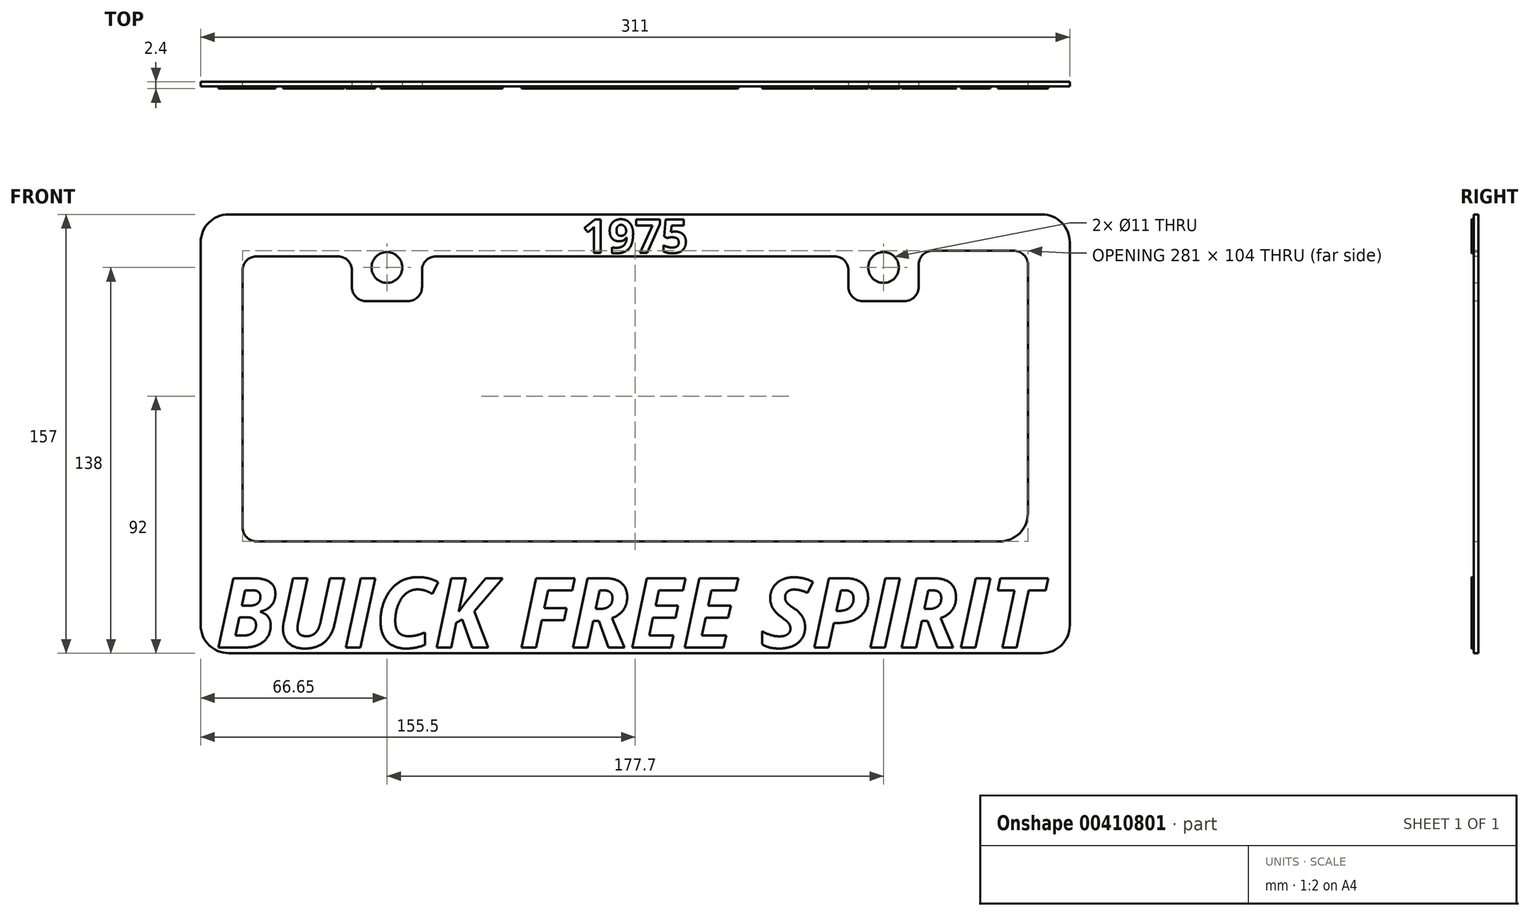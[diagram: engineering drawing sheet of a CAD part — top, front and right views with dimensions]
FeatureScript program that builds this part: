
annotation { "Feature Type Name" : "Feature", "Feature Type Description" : "" }
export const myFeature = defineFeature(function(context is Context, id is Id, definition is map)
    precondition{}
    {
        {
            var Q0;
            Q0=qCreatedBy(makeId("Front.planeOp"),FACE);
            var sketch = newSketch(context, id + "F0", { "sketchPlane" : qUnion([Q0])});
            skLineSegment(sketch, "E0.bottom", {"start": v(145.5, 78.5) * mm, "end": v(-145.5, 78.5) * mm});
            skLineSegment(sketch, "E0.top", {"start": v(145.5, -78.5) * mm, "end": v(-145.5, -78.5) * mm});
            skLineSegment(sketch, "E0.left", {"start": v(155.5, 68.5) * mm, "end": v(155.5, -68.5) * mm});
            skLineSegment(sketch, "E0.right", {"start": v(-155.5, 68.5) * mm, "end": v(-155.5, -68.5) * mm});
            skPoint(sketch, "E0.middle", {"position": v(0, 0) * mm});
            skLineSegment(sketch, "E1.bottom", {"start": v(135.5, 63.5) * mm, "end": v(-135.5, 63.5) * mm});
            skLineSegment(sketch, "E1.left", {"start": v(140.5, 58.5) * mm, "end": v(140.5, -28.5) * mm});
            skLineSegment(sketch, "E1.right", {"start": v(-140.5, 58.5) * mm, "end": v(-140.5, -33.5) * mm});
            skLineSegment(sketch, "E2", {"start": v(-135.5, -38.5) * mm, "end": v(130.5, -38.5) * mm});
            skPoint(sketch, "E3.orphan", {"position": v(140.5, -63.5) * mm});
            skPoint(sketch, "E4.orphan", {"position": v(-140.5, -63.5) * mm});
            skPoint(sketch, "E5.visualSharp", {"position": v(-155.5, 78.5) * mm});
            skArc(sketch, "E5.filletArc", {"start": v(-145.5, 78.5) * mm, "mid": v(-152.57, 75.57) * mm, "end": v(-155.5, 68.5) * mm});
            skPoint(sketch, "E6.visualSharp", {"position": v(-155.5, -78.5) * mm});
            skArc(sketch, "E6.filletArc", {"start": v(-155.5, -68.5) * mm, "mid": v(-152.57, -75.57) * mm, "end": v(-145.5, -78.5) * mm});
            skPoint(sketch, "E7.visualSharp", {"position": v(155.5, 78.5) * mm});
            skArc(sketch, "E7.filletArc", {"start": v(155.5, 68.5) * mm, "mid": v(152.57, 75.57) * mm, "end": v(145.5, 78.5) * mm});
            skPoint(sketch, "E8.visualSharp", {"position": v(155.5, -78.5) * mm});
            skArc(sketch, "E8.filletArc", {"start": v(145.5, -78.5) * mm, "mid": v(152.57, -75.57) * mm, "end": v(155.5, -68.5) * mm});
            skPoint(sketch, "E9.visualSharp", {"position": v(-140.5, 63.5) * mm});
            skArc(sketch, "E9.filletArc", {"start": v(-135.5, 63.5) * mm, "mid": v(-139.04, 62.04) * mm, "end": v(-140.5, 58.5) * mm});
            skPoint(sketch, "E10.visualSharp", {"position": v(-140.5, -38.5) * mm});
            skArc(sketch, "E10.filletArc", {"start": v(-140.5, -33.5) * mm, "mid": v(-139.04, -37.04) * mm, "end": v(-135.5, -38.5) * mm});
            skPoint(sketch, "E11.visualSharp", {"position": v(140.5, -38.5) * mm});
            skArc(sketch, "E11.filletArc", {"start": v(130.5, -38.5) * mm, "mid": v(137.57, -35.57) * mm, "end": v(140.5, -28.5) * mm});
            skPoint(sketch, "E12.visualSharp", {"position": v(140.5, 63.5) * mm});
            skArc(sketch, "E12.filletArc", {"start": v(140.5, 58.5) * mm, "mid": v(139.04, 62.04) * mm, "end": v(135.5, 63.5) * mm});
            skSolve(sketch);
        }
        {
            var Q0;
            Q0=qSketchRegion(id+"F0",true);
            extrude(context, id + "F1", {"entities" : qUnion([Q0]), "depth" : 1.6 * mm});
        }
        {
            var Q0;
            Q0=makeQuery(id+"F1.opExtrude","CAP_FACE",FACE,{"disambiguationData":[OSD([sQuery(id+"F0.wireOp",EDGE,"E0.bottom"),sQuery(id+"F0.wireOp",EDGE,"E0.top"),sQuery(id+"F0.wireOp",EDGE,"E0.left"),sQuery(id+"F0.wireOp",EDGE,"E0.right"),sQuery(id+"F0.wireOp",EDGE,"E1.bottom"),sQuery(id+"F0.wireOp",EDGE,"E1.left"),sQuery(id+"F0.wireOp",EDGE,"E1.right"),sQuery(id+"F0.wireOp",EDGE,"E2"),sQuery(id+"F0.wireOp",EDGE,"E5.filletArc"),sQuery(id+"F0.wireOp",EDGE,"E6.filletArc"),sQuery(id+"F0.wireOp",EDGE,"E7.filletArc"),sQuery(id+"F0.wireOp",EDGE,"E8.filletArc"),sQuery(id+"F0.wireOp",EDGE,"E9.filletArc"),sQuery(id+"F0.wireOp",EDGE,"E10.filletArc"),sQuery(id+"F0.wireOp",EDGE,"E11.filletArc"),sQuery(id+"F0.wireOp",EDGE,"E12.filletArc")])],"isStart":false});
            var sketch = newSketch(context, id + "F2", { "sketchPlane" : qUnion([Q0])});
            skLineSegment(sketch, "E13.bottom", {"start": v(-101.4, 63.5) * mm, "end": v(-76.3, 63.5) * mm});
            skLineSegment(sketch, "E13.top", {"start": v(-101.4, 47.5) * mm, "end": v(-76.3, 47.5) * mm});
            skLineSegment(sketch, "E13.left", {"start": v(-101.4, 63.5) * mm, "end": v(-101.4, 47.5) * mm});
            skLineSegment(sketch, "E13.right", {"start": v(-76.3, 63.5) * mm, "end": v(-76.3, 47.5) * mm});
            skLineSegment(sketch, "E14.bottom", {"start": v(76.3, 63.5) * mm, "end": v(101.4, 63.5) * mm});
            skLineSegment(sketch, "E14.top", {"start": v(76.3, 47.5) * mm, "end": v(101.4, 47.5) * mm});
            skLineSegment(sketch, "E14.left", {"start": v(76.3, 63.5) * mm, "end": v(76.3, 47.5) * mm});
            skLineSegment(sketch, "E14.right", {"start": v(101.4, 63.5) * mm, "end": v(101.4, 47.5) * mm});
            skLineSegment(sketch, "E15", {"start": v(-88.85, 47.5) * mm, "end": v(-88.85, 63.5) * mm, "construction": true});
            skLineSegment(sketch, "E16", {"start": v(-101.4, 47.5) * mm, "end": v(-140.5, 47.5) * mm, "construction": true});
            skLineSegment(sketch, "E17", {"start": v(101.4, 47.5) * mm, "end": v(140.5, 47.5) * mm, "construction": true});
            skSolve(sketch);
        }
        {
            var Q0;
            Q0=qSketchRegion(id+"F2",true);
            var Q1;
            Q1=makeQuery(id+"F1.opExtrude","CAP_FACE",FACE,{"disambiguationData":[OSD([sQuery(id+"F0.wireOp",EDGE,"E0.bottom"),sQuery(id+"F0.wireOp",EDGE,"E0.top"),sQuery(id+"F0.wireOp",EDGE,"E0.left"),sQuery(id+"F0.wireOp",EDGE,"E0.right"),sQuery(id+"F0.wireOp",EDGE,"E1.bottom"),sQuery(id+"F0.wireOp",EDGE,"E1.left"),sQuery(id+"F0.wireOp",EDGE,"E1.right"),sQuery(id+"F0.wireOp",EDGE,"E2"),sQuery(id+"F0.wireOp",EDGE,"E5.filletArc"),sQuery(id+"F0.wireOp",EDGE,"E6.filletArc"),sQuery(id+"F0.wireOp",EDGE,"E7.filletArc"),sQuery(id+"F0.wireOp",EDGE,"E8.filletArc"),sQuery(id+"F0.wireOp",EDGE,"E9.filletArc"),sQuery(id+"F0.wireOp",EDGE,"E10.filletArc"),sQuery(id+"F0.wireOp",EDGE,"E11.filletArc"),sQuery(id+"F0.wireOp",EDGE,"E12.filletArc")])],"isStart":true});
            extrude(context, id + "F3", {"entities" : qUnion([Q0]), "operationType" : NewBodyOperationType.ADD, "endBound" : BoundingType.UP_TO_SURFACE, "oppositeDirection" : true, "endBoundEntityFace" : qUnion([Q1]), "depth" : 25 * mm});
        }
        {
            var Q0;
            Q0=makeQuery(id+"F3.opExtrude","SWEPT_EDGE",EDGE,{"disambiguationData":[OSD([sQuery(id+"F2.wireOp",EDGE,"E13.top"),sQuery(id+"F2.wireOp",EDGE,"E13.left")])]});
            var Q1;
            Q1=makeQuery(id+"F3.opExtrude","SWEPT_EDGE",EDGE,{"disambiguationData":[OSD([sQuery(id+"F0.wireOp",EDGE,"E1.bottom"),sQuery(id+"F2.wireOp",EDGE,"E13.bottom"),sQuery(id+"F2.wireOp",EDGE,"E13.left")])]});
            var Q2;
            Q2=makeQuery(id+"F3.opExtrude","SWEPT_EDGE",EDGE,{"disambiguationData":[OSD([sQuery(id+"F2.wireOp",EDGE,"E13.top"),sQuery(id+"F2.wireOp",EDGE,"E13.right")])]});
            var Q3;
            Q3=makeQuery(id+"F3.opExtrude","SWEPT_EDGE",EDGE,{"disambiguationData":[OSD([sQuery(id+"F0.wireOp",EDGE,"E1.bottom"),sQuery(id+"F2.wireOp",EDGE,"E13.bottom"),sQuery(id+"F2.wireOp",EDGE,"E13.right")])]});
            var Q4;
            Q4=makeQuery(id+"F3.opExtrude","SWEPT_EDGE",EDGE,{"disambiguationData":[OSD([sQuery(id+"F2.wireOp",EDGE,"E14.top"),sQuery(id+"F2.wireOp",EDGE,"E14.right")])]});
            var Q5;
            Q5=makeQuery(id+"F3.opExtrude","SWEPT_EDGE",EDGE,{"disambiguationData":[OSD([sQuery(id+"F0.wireOp",EDGE,"E1.bottom"),sQuery(id+"F2.wireOp",EDGE,"E14.bottom"),sQuery(id+"F2.wireOp",EDGE,"E14.right")])]});
            var Q6;
            Q6=makeQuery(id+"F3.opExtrude","SWEPT_EDGE",EDGE,{"disambiguationData":[OSD([sQuery(id+"F2.wireOp",EDGE,"E14.top"),sQuery(id+"F2.wireOp",EDGE,"E14.left")])]});
            var Q7;
            Q7=makeQuery(id+"F3.opExtrude","SWEPT_EDGE",EDGE,{"disambiguationData":[OSD([sQuery(id+"F0.wireOp",EDGE,"E1.bottom"),sQuery(id+"F2.wireOp",EDGE,"E14.bottom"),sQuery(id+"F2.wireOp",EDGE,"E14.left")])]});
            fillet(context, id + "F4", {"entities" : qUnion([Q0, Q1, Q2, Q3, Q4, Q5, Q6, Q7]), "radius" : 5 * mm, "tangentPropagation" : true, "allowEdgeOverflow" : false});
        }
        {
            var Q0;
            Q0=makeQuery(id+"F3.boolean.opBoolean","MERGE",FACE,{"derivedFrom":[makeQuery(id+"F1.opExtrude","CAP_FACE",FACE,{"disambiguationData":[OSD([sQuery(id+"F0.wireOp",EDGE,"E0.bottom"),sQuery(id+"F0.wireOp",EDGE,"E0.top"),sQuery(id+"F0.wireOp",EDGE,"E0.left"),sQuery(id+"F0.wireOp",EDGE,"E0.right"),sQuery(id+"F0.wireOp",EDGE,"E1.bottom"),sQuery(id+"F0.wireOp",EDGE,"E1.left"),sQuery(id+"F0.wireOp",EDGE,"E1.right"),sQuery(id+"F0.wireOp",EDGE,"E2"),sQuery(id+"F0.wireOp",EDGE,"E5.filletArc"),sQuery(id+"F0.wireOp",EDGE,"E6.filletArc"),sQuery(id+"F0.wireOp",EDGE,"E7.filletArc"),sQuery(id+"F0.wireOp",EDGE,"E8.filletArc"),sQuery(id+"F0.wireOp",EDGE,"E9.filletArc"),sQuery(id+"F0.wireOp",EDGE,"E10.filletArc"),sQuery(id+"F0.wireOp",EDGE,"E11.filletArc"),sQuery(id+"F0.wireOp",EDGE,"E12.filletArc")])],"isStart":false}),makeQuery(id+"F3.opExtrude","CAP_FACE",FACE,{"disambiguationData":[OSD([sQuery(id+"F2.wireOp",EDGE,"E13.bottom"),sQuery(id+"F2.wireOp",EDGE,"E13.top"),sQuery(id+"F2.wireOp",EDGE,"E13.left"),sQuery(id+"F2.wireOp",EDGE,"E13.right")])],"isStart":true}),makeQuery(id+"F3.opExtrude","CAP_FACE",FACE,{"disambiguationData":[OSD([sQuery(id+"F2.wireOp",EDGE,"E14.bottom"),sQuery(id+"F2.wireOp",EDGE,"E14.top"),sQuery(id+"F2.wireOp",EDGE,"E14.left"),sQuery(id+"F2.wireOp",EDGE,"E14.right")])],"isStart":true})]});
            var sketch = newSketch(context, id + "F5", { "sketchPlane" : qUnion([Q0])});
            skLineSegment(sketch, "E18", {"start": v(140.5, 58.5) * mm, "end": v(140.5, 65.5) * mm});
            skLineSegment(sketch, "E19", {"start": v(140.5, 65.5) * mm, "end": v(101.4, 65.5) * mm});
            skPoint(sketch, "E20.endSnap0", {"position": v(102.86, 62.04) * mm});
            skLineSegment(sketch, "E21", {"start": v(101.4, 58.5) * mm, "end": v(101.4, 65.5) * mm});
            skLineSegment(sketch, "E22", {"start": v(101.4, 58.5) * mm, "end": v(140.5, 58.5) * mm});
            skSolve(sketch);
        }
        {
            var Q0;
            Q0=qSketchRegion(id+"F5",true);
            extrude(context, id + "F6", {"entities" : qUnion([Q0]), "operationType" : NewBodyOperationType.REMOVE, "oppositeDirection" : true, "depth" : 25 * mm});
        }
        {
            var Q0;
            Q0=makeQuery(id+"F6.boolean.opBoolean","COPY",EDGE,{"derivedFrom":makeQuery(id+"F6.opExtrude","SWEPT_EDGE",EDGE,{"disambiguationData":[OSD([sQuery(id+"F5.wireOp",EDGE,"E19"),sQuery(id+"F5.wireOp",EDGE,"E21")])]})});
            var Q1;
            Q1=makeQuery(id+"F6.boolean.opBoolean","COPY",EDGE,{"derivedFrom":makeQuery(id+"F6.opExtrude","SWEPT_EDGE",EDGE,{"disambiguationData":[OSD([sQuery(id+"F5.wireOp",EDGE,"E18"),sQuery(id+"F5.wireOp",EDGE,"E19")])]})});
            fillet(context, id + "F7", {"entities" : qUnion([Q0, Q1]), "radius" : 5 * mm, "tangentPropagation" : true, "allowEdgeOverflow" : false});
        }
        {
            var Q0;
            Q0=makeQuery(id+"F3.boolean.opBoolean","MERGE",FACE,{"derivedFrom":[makeQuery(id+"F1.opExtrude","CAP_FACE",FACE,{"disambiguationData":[OSD([sQuery(id+"F0.wireOp",EDGE,"E0.bottom"),sQuery(id+"F0.wireOp",EDGE,"E0.top"),sQuery(id+"F0.wireOp",EDGE,"E0.left"),sQuery(id+"F0.wireOp",EDGE,"E0.right"),sQuery(id+"F0.wireOp",EDGE,"E1.bottom"),sQuery(id+"F0.wireOp",EDGE,"E1.left"),sQuery(id+"F0.wireOp",EDGE,"E1.right"),sQuery(id+"F0.wireOp",EDGE,"E2"),sQuery(id+"F0.wireOp",EDGE,"E5.filletArc"),sQuery(id+"F0.wireOp",EDGE,"E6.filletArc"),sQuery(id+"F0.wireOp",EDGE,"E7.filletArc"),sQuery(id+"F0.wireOp",EDGE,"E8.filletArc"),sQuery(id+"F0.wireOp",EDGE,"E9.filletArc"),sQuery(id+"F0.wireOp",EDGE,"E10.filletArc"),sQuery(id+"F0.wireOp",EDGE,"E11.filletArc"),sQuery(id+"F0.wireOp",EDGE,"E12.filletArc")])],"isStart":false}),makeQuery(id+"F3.opExtrude","CAP_FACE",FACE,{"disambiguationData":[OSD([sQuery(id+"F2.wireOp",EDGE,"E13.bottom"),sQuery(id+"F2.wireOp",EDGE,"E13.top"),sQuery(id+"F2.wireOp",EDGE,"E13.left"),sQuery(id+"F2.wireOp",EDGE,"E13.right")])],"isStart":true}),makeQuery(id+"F3.opExtrude","CAP_FACE",FACE,{"disambiguationData":[OSD([sQuery(id+"F2.wireOp",EDGE,"E14.bottom"),sQuery(id+"F2.wireOp",EDGE,"E14.top"),sQuery(id+"F2.wireOp",EDGE,"E14.left"),sQuery(id+"F2.wireOp",EDGE,"E14.right")])],"isStart":true})]});
            var sketch = newSketch(context, id + "F8", { "sketchPlane" : qUnion([Q0])});
            skCircle(sketch, "E23", {"center": v(-88.85, 59.5) * mm, "radius": 5.5 * mm});
            skCircle(sketch, "E24", {"center": v(88.85, 59.5) * mm, "radius": 5.5 * mm});
            skLineSegment(sketch, "E25", {"start": v(-88.85, 47.5) * mm, "end": v(-88.85, 92.98) * mm, "construction": true});
            skLineSegment(sketch, "E26", {"start": v(88.85, 47.5) * mm, "end": v(88.85, 70.92) * mm, "construction": true});
            skSolve(sketch);
        }
        {
            var Q0;
            Q0=qSketchRegion(id+"F8",true);
            extrude(context, id + "F9", {"entities" : qUnion([Q0]), "operationType" : NewBodyOperationType.REMOVE, "oppositeDirection" : true, "depth" : 25 * mm});
        }
        {
            var Q0;
            Q0=makeQuery(id+"F3.boolean.opBoolean","MERGE",FACE,{"derivedFrom":[makeQuery(id+"F1.opExtrude","CAP_FACE",FACE,{"disambiguationData":[OSD([sQuery(id+"F0.wireOp",EDGE,"E0.bottom"),sQuery(id+"F0.wireOp",EDGE,"E0.top"),sQuery(id+"F0.wireOp",EDGE,"E0.left"),sQuery(id+"F0.wireOp",EDGE,"E0.right"),sQuery(id+"F0.wireOp",EDGE,"E1.bottom"),sQuery(id+"F0.wireOp",EDGE,"E1.left"),sQuery(id+"F0.wireOp",EDGE,"E1.right"),sQuery(id+"F0.wireOp",EDGE,"E2"),sQuery(id+"F0.wireOp",EDGE,"E5.filletArc"),sQuery(id+"F0.wireOp",EDGE,"E6.filletArc"),sQuery(id+"F0.wireOp",EDGE,"E7.filletArc"),sQuery(id+"F0.wireOp",EDGE,"E8.filletArc"),sQuery(id+"F0.wireOp",EDGE,"E9.filletArc"),sQuery(id+"F0.wireOp",EDGE,"E10.filletArc"),sQuery(id+"F0.wireOp",EDGE,"E11.filletArc"),sQuery(id+"F0.wireOp",EDGE,"E12.filletArc")])],"isStart":false}),makeQuery(id+"F3.opExtrude","CAP_FACE",FACE,{"disambiguationData":[OSD([sQuery(id+"F2.wireOp",EDGE,"E13.bottom"),sQuery(id+"F2.wireOp",EDGE,"E13.top"),sQuery(id+"F2.wireOp",EDGE,"E13.left"),sQuery(id+"F2.wireOp",EDGE,"E13.right")])],"isStart":true}),makeQuery(id+"F3.opExtrude","CAP_FACE",FACE,{"disambiguationData":[OSD([sQuery(id+"F2.wireOp",EDGE,"E14.bottom"),sQuery(id+"F2.wireOp",EDGE,"E14.top"),sQuery(id+"F2.wireOp",EDGE,"E14.left"),sQuery(id+"F2.wireOp",EDGE,"E14.right")])],"isStart":true})]});
            var sketch = newSketch(context, id + "F10", { "sketchPlane" : qUnion([Q0])});
            skText(sketch, "E27", { "text": "1975", "fontName": "OpenSans-Bold.ttf"});
            const initialGuessF10  = {"E27": [-0.0192, 0.06475, 1, 0, 0.012]};
            skSetInitialGuess(sketch, initialGuessF10);
            skSolve(sketch);
        }
        {
            var Q0;
            Q0=qSketchRegion(id+"F10",true);
            extrude(context, id + "F11", {"entities" : qUnion([Q0]), "operationType" : NewBodyOperationType.ADD, "depth" : .8 * mm});
        }
        {
            var Q0;
            {var subQ0=sQuery(id+"F0.wireOp",EDGE,"E0.right");var subQ2=sQuery(id+"F2.wireOp",EDGE,"E14.left");var subQ3=sQuery(id+"F2.wireOp",EDGE,"E14.bottom");var subQ4=sQuery(id+"F0.wireOp",EDGE,"E1.bottom");var subQ5=sQuery(id+"F2.wireOp",EDGE,"E14.right");var subQ6=sQuery(id+"F2.wireOp",EDGE,"E14.top");var subQ7=sQuery(id+"F0.wireOp",EDGE,"E8.filletArc");var subQ8=sQuery(id+"F0.wireOp",EDGE,"E5.filletArc");var subQ9=sQuery(id+"F0.wireOp",EDGE,"E7.filletArc");var subQ10=sQuery(id+"F0.wireOp",EDGE,"E2");var subQ11=sQuery(id+"F0.wireOp",EDGE,"E6.filletArc");var subQ12=sQuery(id+"F0.wireOp",EDGE,"E1.right");var subQ13=sQuery(id+"F2.wireOp",EDGE,"E13.right");var subQ14=sQuery(id+"F2.wireOp",EDGE,"E13.top");var subQ15=sQuery(id+"F0.wireOp",EDGE,"E1.left");var subQ16=sQuery(id+"F0.wireOp",EDGE,"E9.filletArc");var subQ17=sQuery(id+"F2.wireOp",EDGE,"E13.bottom");var subQ18=sQuery(id+"F0.wireOp",EDGE,"E0.bottom");var subQ19=sQuery(id+"F0.wireOp",EDGE,"E0.top");var subQ20=sQuery(id+"F0.wireOp",EDGE,"E0.left");var subQ21=sQuery(id+"F0.wireOp",EDGE,"E10.filletArc");var subQ23=sQuery(id+"F2.wireOp",EDGE,"E13.left");var subQ24=sQuery(id+"F0.wireOp",EDGE,"E11.filletArc");Q0=makeQuery(id+"F11.boolean.opBoolean","SPLIT",FACE,{"disambiguationData":[TD([makeQuery(id+"F1.opExtrude","SWEPT_FACE",FACE,{"disambiguationData":[OSD([subQ18])]})])],"derivedFrom":makeQuery(id+"F3.boolean.opBoolean","MERGE",FACE,{"derivedFrom":[makeQuery(id+"F1.opExtrude","CAP_FACE",FACE,{"disambiguationData":[OSD([subQ18,subQ19,subQ20,subQ0,subQ4,subQ15,subQ12,subQ10,subQ8,subQ11,subQ9,subQ7,subQ16,subQ21,subQ24,sQuery(id+"F0.wireOp",EDGE,"E12.filletArc")])],"isStart":false}),makeQuery(id+"F3.opExtrude","CAP_FACE",FACE,{"disambiguationData":[OSD([subQ17,subQ14,subQ23,subQ13])],"isStart":true}),makeQuery(id+"F3.opExtrude","CAP_FACE",FACE,{"disambiguationData":[OSD([subQ3,subQ6,subQ2,subQ5])],"isStart":true})]})});}
            var sketch = newSketch(context, id + "F12", { "sketchPlane" : qUnion([Q0])});
            skText(sketch, "E28", { "text": "BUICK FREE SPIRIT", "fontName": "OpenSans-BoldItalic.ttf"});
            const initialGuessF12  = {"E28": [-0.15, -0.0765, 1, 0, 0.02503]};
            skSetInitialGuess(sketch, initialGuessF12);
            skSolve(sketch);
        }
        {
            var Q0;
            Q0=qSketchRegion(id+"F12",true);
            extrude(context, id + "F13", {"entities" : qUnion([Q0]), "operationType" : NewBodyOperationType.ADD, "depth" : .8 * mm});
        }
    });
